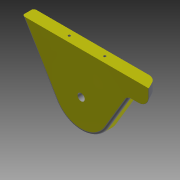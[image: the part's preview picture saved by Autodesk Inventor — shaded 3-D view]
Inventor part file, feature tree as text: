
AUTODESK INVENTOR PART (.ipt)
format: ipt  version: 2015 (Build 190159000, 159)  size: 195,072 bytes
history: native  units: mm
features: extrude x5, sketch x5, fillet x4
ambient origin geometry x8: Origin, YZ Plane, XZ Plane, XY Plane, X Axis, Y Axis, Z Axis, Center Point
bodies: Solid1 (feature_tree)
feature tree (14):
  extrude  "Extrusion1"  Depth=50.0mm
  extrude  "Extrusion2"  Depth=6.0mm
  extrude  "Extrusion3"  Depth=2.0mm
  extrude  "Extrusion4"  Depth=10.0mm TaperAngle=0.0deg
  extrude  "Extrusion5"  Depth=10.0mm
  fillet  "Fillet1"  Radius=10.0mm
  fillet  "Fillet2"  Radius=6.4mm
  fillet  "Fillet3"  Radius=48.5mm
  fillet  "Fillet4"  [1 undecoded]
  sketch  "Sketch1"  dims[d4=50.0mm d5=50.0mm]
  sketch  "Sketch2"  dims[d6=100.0mm d7=6.0mm]
  sketch  "Sketch3"  dims[d8=10.0mm d9=0.0mm d11=2.0mm]
  sketch  "Sketch4"  dims[d12=2.0mm d13=10.0mm d14=0.0mm]
  sketch  "Sketch5"  dims[d15=15.0mm d16=10.0mm d17=10.0mm d18=0.0mm d19=6.4mm d20=0.0mm d21=48.5mm d22=90.0deg d23=124.0mm d24=15.0mm d25=0.0mm d26=8.0mm d27=8.0mm d28=2.0mm d29=0.2mm]
note: 1 required parameter value undecoded (feature->parameter linkage not recoverable at this tier; creation-order binding heuristic only, values carry confidence <= 0.55)
